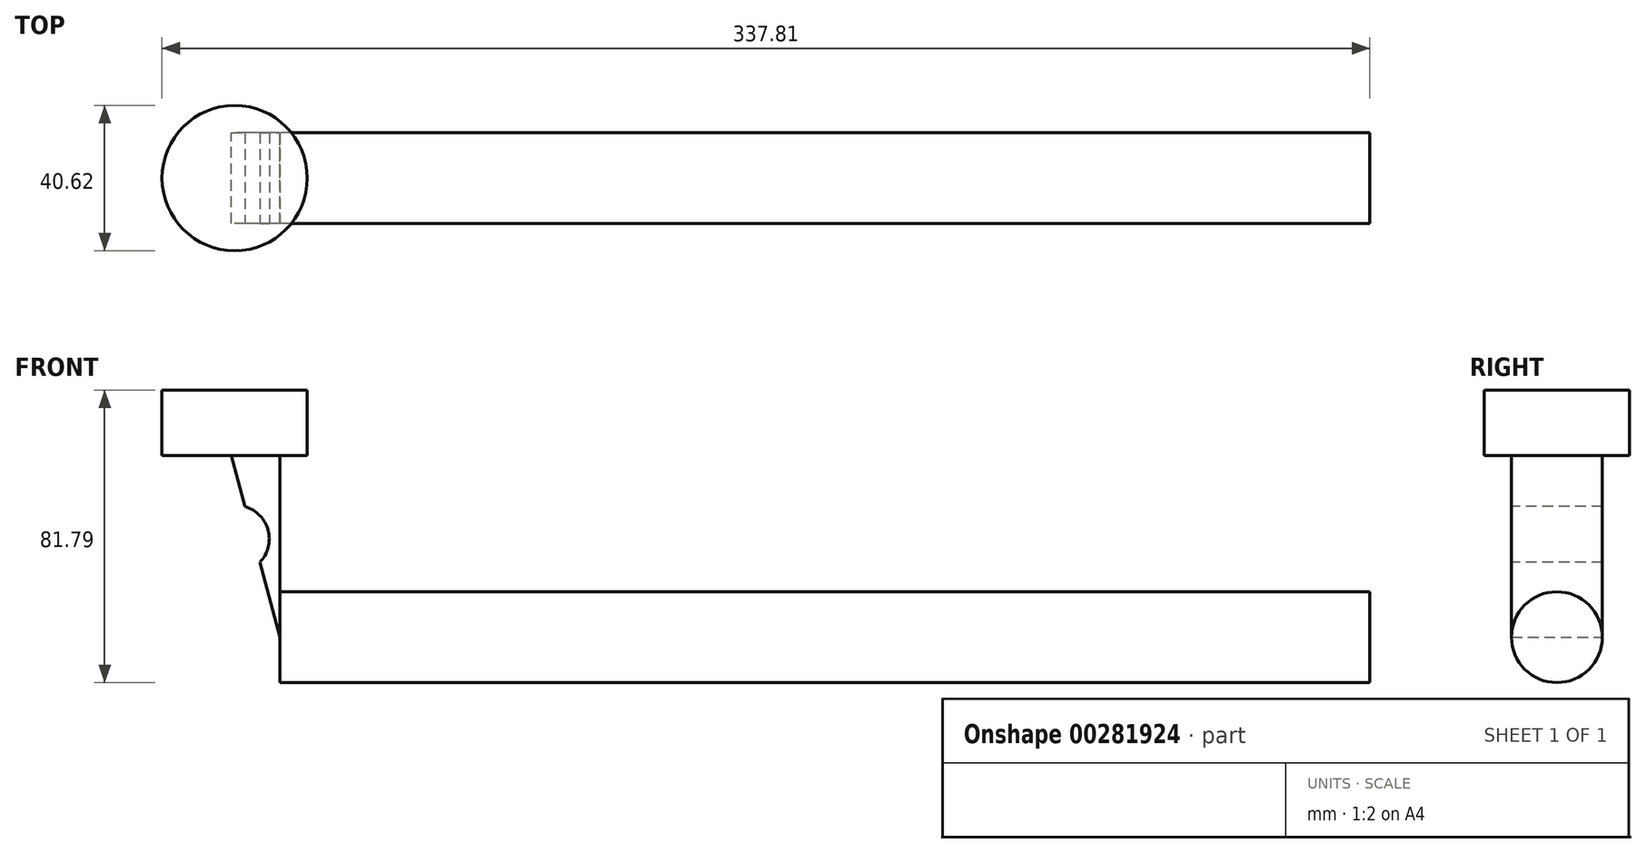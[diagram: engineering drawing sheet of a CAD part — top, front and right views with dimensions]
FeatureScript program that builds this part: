
annotation { "Feature Type Name" : "Feature", "Feature Type Description" : "" }
export const myFeature = defineFeature(function(context is Context, id is Id, definition is map)
    precondition{}
    {
        {
            var Q0;
            Q0=qCreatedBy(makeId("Front.planeOp"),FACE);
            var sketch = newSketch(context, id + "F0", { "sketchPlane" : qUnion([Q0])});
            skLineSegment(sketch, "E0.bottom", {"start": v(-30.93, 0) * mm, "end": v(273.87, 0) * mm});
            skLineSegment(sketch, "E0.top", {"start": v(-30.93, 12.7) * mm, "end": v(273.87, 12.7) * mm});
            skLineSegment(sketch, "E0.left", {"start": v(-30.93, 0) * mm, "end": v(-30.93, 12.7) * mm});
            skLineSegment(sketch, "E0.right", {"start": v(273.87, 0) * mm, "end": v(273.87, 12.7) * mm});
            skLineSegment(sketch, "E1.bottom", {"start": v(-30.93, 0) * mm, "end": v(-56.33, 0) * mm});
            skLineSegment(sketch, "E1.top", {"start": v(-30.93, 50.8) * mm, "end": v(-56.33, 50.8) * mm});
            skLineSegment(sketch, "E1.left", {"start": v(-30.93, 0) * mm, "end": v(-30.93, 50.8) * mm});
            skLineSegment(sketch, "E1.right", {"start": v(-56.33, 0) * mm, "end": v(-56.33, 50.8) * mm});
            skLineSegment(sketch, "E2.bottom", {"start": v(-56.33, 0) * mm, "end": v(-30.93, 0) * mm});
            skLineSegment(sketch, "E2.top", {"start": v(-56.33, -76.2) * mm, "end": v(-30.93, -76.2) * mm});
            skLineSegment(sketch, "E2.left", {"start": v(-56.33, 0) * mm, "end": v(-56.33, -76.2) * mm});
            skLineSegment(sketch, "E2.right", {"start": v(-30.93, 0) * mm, "end": v(-30.93, -76.2) * mm});
            skSolve(sketch);
        }
        {
            var Q0;
            {var subQ0=sQuery(id+"F0.wireOp",EDGE,"E0.bottom");Q0=makeQuery(id+"F0.imprint","IMPRINT",FACE,{"disambiguationData":[TD([[makeQuery(id+"F0.imprint","IMPRINT",EDGE,{"derivedFrom":subQ0}),1.0]])]});}
            var Q1;
            Q1=sQuery(id+"F0.wireOp",EDGE,"E0.bottom");
            revolve(context, id + "F1", {"entities" : qUnion([Q0]), "axis" : qUnion([Q1]), "revolveType" : RevolveType.FULL});
        }
        {
            var Q0;
            {var subQ2=sQuery(id+"F0.wireOp",EDGE,"E1.top");Q0=makeQuery(id+"F0.imprint","IMPRINT",FACE,{"disambiguationData":[TD([[makeQuery(id+"F0.imprint","IMPRINT",EDGE,{"derivedFrom":subQ2}),1.0]])]});}
            var Q1;
            Q1=makeQuery(id+"F0.imprint","IMPRINT",FACE,{"disambiguationData":[TD([[makeQuery(id+"F0.imprint","IMPRINT",EDGE,{"derivedFrom":sQuery(id+"F0.wireOp",EDGE,"E2.bottom")}),-1.0]])]});
            extrude(context, id + "F2", {"entities" : qUnion([Q0, Q1]), "operationType" : NewBodyOperationType.ADD, "endBound" : BoundingType.SYMMETRIC, "depth" : 25.4 * mm});
        }
        {
            var Q0;
            Q0=makeQuery(id+"F2.opExtrude","SWEPT_EDGE",EDGE,{"disambiguationData":[OSD([sQuery(id+"F0.wireOp",EDGE,"E2.top"),sQuery(id+"F0.wireOp",EDGE,"E2.left")])]});
            chamfer(context, id + "F3", {"entities" : qUnion([Q0]), "chamferType" : ChamferType.OFFSET_ANGLE, "width" : 25.4 * mm, "oppositeDirection" : false, "angle" : 75 * degree, "tangentPropagation" : true});
        }
        {
            var Q0;
            Q0=makeQuery(id+"F2.opExtrude","SWEPT_FACE",FACE,{"disambiguationData":[OSD([sQuery(id+"F0.wireOp",EDGE,"E1.top")])]});
            var sketch = newSketch(context, id + "F4", { "sketchPlane" : qUnion([Q0])});
            skCircle(sketch, "E3", {"center": v(-43.63, 0) * mm, "radius": 20.3 * mm});
            skPoint(sketch, "E3.centerSnap0", {"position": v(-43.63, 12.7) * mm});
            skSolve(sketch);
        }
        {
            var Q0;
            Q0=makeQuery(id+"F4.imprint","IMPRINT",FACE,{"disambiguationData":[TD([[makeQuery(id+"F4.imprint","IMPRINT",EDGE,{"derivedFrom":sQuery(id+"F4.wireOp",EDGE,"E3")}),1.0]])]});
            var Q1;
            {var subQ0=sQuery(id+"F0.wireOp",EDGE,"E1.top");Q1=makeQuery(id+"F4.imprint","IMPRINT",FACE,{"disambiguationData":[TD([[makeQuery(id+"F4.imprint","IMPRINT",EDGE,{"derivedFrom":makeQuery(id+"F2.opExtrude","CAP_EDGE",EDGE,{"disambiguationData":[OSD([subQ0])],"isStart":true})}),1.0]])]});}
            extrude(context, id + "F5", {"entities" : qUnion([Q0, Q1]), "operationType" : NewBodyOperationType.ADD, "depth" : 18.29 * mm});
        }
        {
            var Q0;
            Q0=makeQuery(id+"F2.opExtrude","CAP_FACE",FACE,{"disambiguationData":[OSD([sQuery(id+"F0.wireOp",EDGE,"E1.top"),sQuery(id+"F0.wireOp",EDGE,"E1.left"),sQuery(id+"F0.wireOp",EDGE,"E1.right"),sQuery(id+"F0.wireOp",EDGE,"E2.top"),sQuery(id+"F0.wireOp",EDGE,"E2.left"),sQuery(id+"F0.wireOp",EDGE,"E2.right")])],"isStart":false});
            var sketch = newSketch(context, id + "F6", { "sketchPlane" : qUnion([Q0])});
            skCircle(sketch, "E4", {"center": v(-43.42, 27.45) * mm, "radius": 9.48 * mm});
            skSolve(sketch);
        }
        {
            var Q0;
            Q0=makeQuery(id+"F6.imprint","IMPRINT",FACE,{"disambiguationData":[TD([[makeQuery(id+"F6.imprint","IMPRINT",EDGE,{"derivedFrom":sQuery(id+"F6.wireOp",EDGE,"E4")}),1.0]])]});
            extrude(context, id + "F7", {"entities" : qUnion([Q0]), "operationType" : NewBodyOperationType.REMOVE, "oppositeDirection" : true, "depth" : 25.4 * mm});
        }
    });
